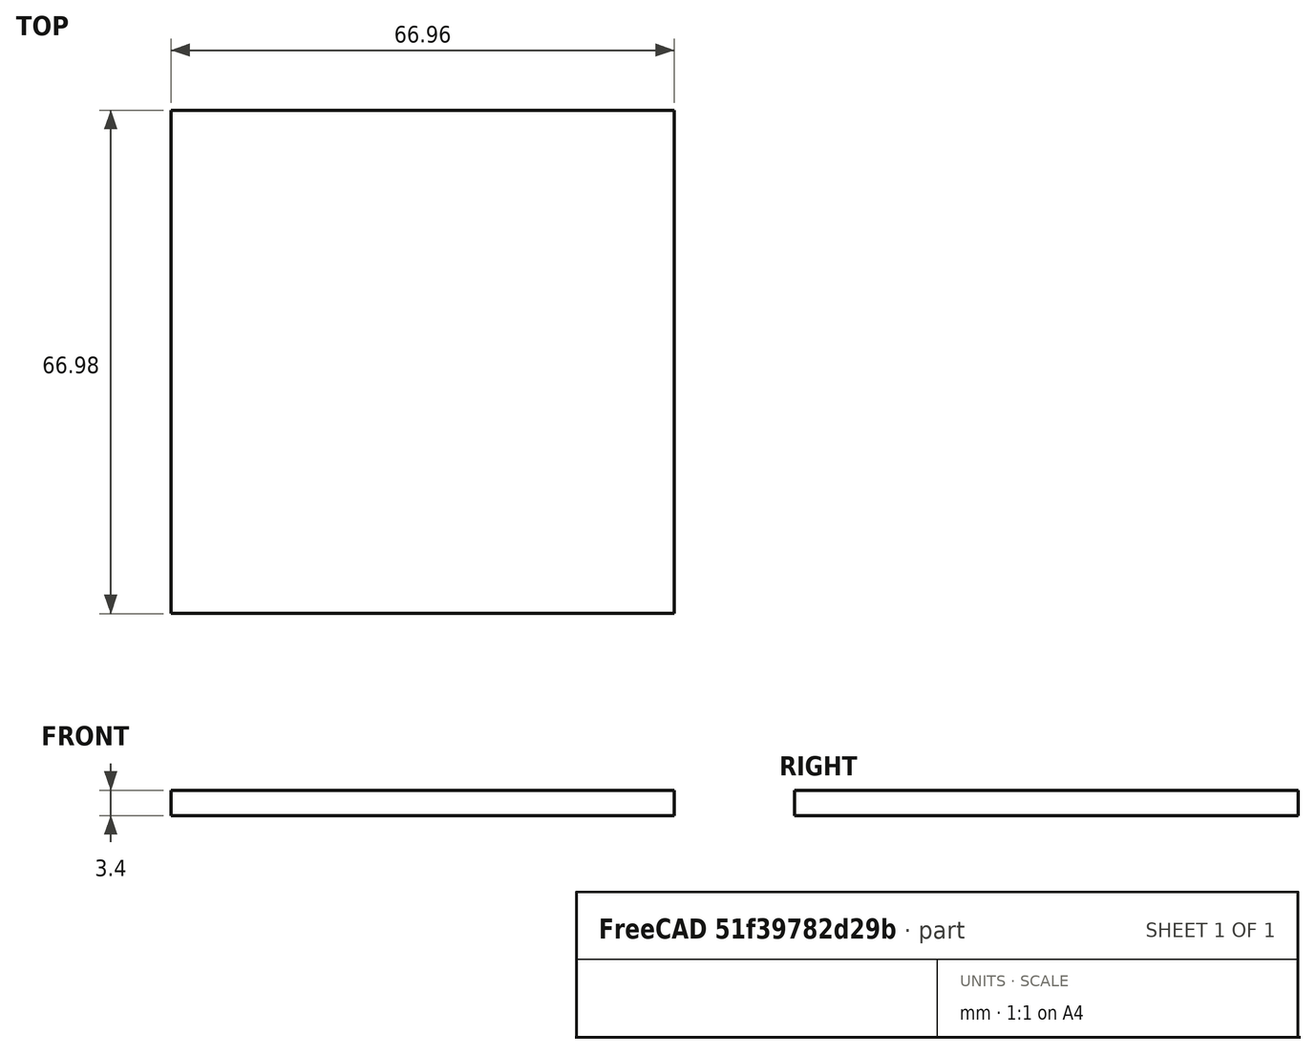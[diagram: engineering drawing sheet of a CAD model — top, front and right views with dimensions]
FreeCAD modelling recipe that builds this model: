
FCSTD DOCUMENT  (FreeCAD 0.17R12703 (Git))
Label: Servospant
License: All rights reserved
LicenseURL: http://en.wikipedia.org/wiki/All_rights_reserved
objects: Path::FeaturePython×8, Part::FeaturePython×2, Part::Feature×1, App::FeaturePython×1, Path::FeatureCompoundPython×1
note: 5 computed .brp shape members not serialized (recipe doc carries the construction recipe); baked Part::Feature solids carry a one-line shape summary decoded from their .brp

FEATURE [Part::Feature] Part__Feature  label="Servospant"
  Placement = pos=(0,0,-3.4) rot=(0,0,1;0rad)
  shape: bbox 66.96 x 67 x 3.4 mm, 43 faces (baked)
FEATURE [App::FeaturePython] SetupSheet  # Path/CAM operation (typed FeaturePython)
  ClearanceHeightExpression = StartDepth+SetupSheet.ClearanceHeightOffset
  ClearanceHeightOffset = 5
  FinalDepthExpression = OpFinalDepth
  HorizRapid = 0
  SafeHeightExpression = StartDepth+SetupSheet.SafeHeightOffset
  SafeHeightOffset = 3
  StartDepthExpression = OpStartDepth
  StepDownExpression = OpToolDiameter
  VertRapid = 0
FEATURE [Part::FeaturePython] Clone  label="Base-Servospant"  # Draft clone (typed FeaturePython)
  AttacherType = Attacher::AttachEngine3D
  Fuse = false
  Objects = -> [Part__Feature]
  PathResource = Base
  Placement = pos=(0,0,-3.4) rot=(0,0,1;0rad)
  Scale = (1,1,1)
FEATURE [Path::FeaturePython] T1__Schaftfraeser_D2  label="T1: Schaftfraeser_D2"  # Path/CAM operation (typed FeaturePython)
  HorizFeed = 400
  HorizRapid = 0
  SpindleDir = 0
  SpindleSpeed = 0
  ToolNumber = 1
  VertFeed = 100
  VertRapid = 0
  expr: VertRapid = SetupSheet.VertRapid
  expr: HorizRapid = SetupSheet.HorizRapid
FEATURE [Part::FeaturePython] Stock  # WARN: FeaturePython — macro-defined, semantics opaque (R4)
  Base = -> Part__Feature
  ExtXneg = 0
  ExtXpos = 0
  ExtYneg = 0
  ExtYpos = 0
  ExtZneg = 0
  ExtZpos = 0
  StockType = FromBase
FEATURE [Path::FeaturePython] Profile_Edges  # Path/CAM operation (typed FeaturePython)
  Active = true
  AreaParams:
    OpenMode = 0
    Angle = 45.0
    MinArcPoints = 4
    Coplanar = 0
    Tolerance = 1e-07
    CleanDistance = 0.0
    PocketExtraOffset = 0.0
    AngleShift = 0.0
    SubjectFill = 0
    RoundPreceision = 0.0
    Simplify = False
    SectionTolerance = 1e-06
    MaxArcPoints = 100
    SectionOffset = 0.0
    Offset = -1.0
    Accuracy = 0.01
    PocketStepover = 0.0
    ClipFill = 0
    ToolRadius = 1.0
    Outline = False
    ClipperScale = 10000000.0
    FromCenter = False
    Explode = False
    EndType = 0
    Shift = 0.0
    ExtraPass = 0
    Project = False
    JoinType = 0
    Thicken = False
    Stepdown = 1.0
    SectionMode = 2
    MiterLimit = 2.0
    Deflection = 0.01
    Reorient = True
    FitArcs = True
    SectionCount = -1
    PocketMode = 0
    Stepover = 0.0
    Unit = 1.0
    Fill = 0
  Base = -> [Clone]
  ClearanceHeight = 5
  Direction = 0
  FinalDepth = -3.7
  JoinType = 0
  MiterLimit = 0.1
  OffsetExtra = 0
  OpFinalDepth = 0
  OpStartDepth = 2
  OpToolDiameter = 2
  PathParams = {'resume_height': 3.0, 'feedrate': 400.0, 'verbose': True, 'orientation': 1, 'return_end': True, 'preamble': False, 'retraction': 5.0, 'feedrate_v': 100.0}
  SafeHeight = 3
  Side = 1
  StartDepth = 0
  StartPoint = (0,0,0)
  StepDown = 2
  ToolController = -> T1__Schaftfraeser_D2
  UseComp = true
  UseStartPoint = false
  expr: ClearanceHeight = StartDepth + SetupSheet.ClearanceHeightOffset
  expr: SafeHeight = StartDepth + SetupSheet.SafeHeightOffset
  expr: StepDown = 2
  expr: FinalDepth = -3.7000000000000002
  expr: StartDepth = 0
FEATURE [Path::FeaturePython] DogboneDressup  # Path/CAM operation (typed FeaturePython)
  Base = -> Profile_Edges
  Custom = 0
  Incision = 0
  Side = 0
  Style = 0
  ToolController = -> T1__Schaftfraeser_D2
FEATURE [Path::FeaturePython] TagDressup  # Path/CAM operation (typed FeaturePython)
  Angle = 45
  Base = -> DogboneDressup
  Height = 1.6
  Positions = (2) [(-6.83404,-25.6047,0),(9.97059,24.5455,0)]
  Radius = 0
  SegmentationFactor = 50
  Width = 4
FEATURE [Path::FeaturePython] Contour  # Path/CAM operation (typed FeaturePython)
  Active = true
  AreaParams:
    OpenMode = 0
    Angle = 45.0
    MinArcPoints = 4
    Coplanar = 2
    Tolerance = 1e-07
    CleanDistance = 0.0
    PocketExtraOffset = 0.0
    AngleShift = 0.0
    SubjectFill = 0
    RoundPreceision = 0.0
    Simplify = False
    SectionTolerance = 1e-06
    MaxArcPoints = 100
    SectionOffset = 0.0
    Offset = 1.0
    Accuracy = 0.01
    PocketStepover = 0.0
    ClipFill = 0
    ToolRadius = 1.0
    Outline = False
    ClipperScale = 10000000.0
    FromCenter = False
    Explode = False
    EndType = 0
    Shift = 0.0
    ExtraPass = 0
    Project = False
    JoinType = 0
    Thicken = False
    Stepdown = 1.0
    SectionMode = 2
    MiterLimit = 2.0
    Deflection = 0.01
    Reorient = True
    FitArcs = True
    SectionCount = -1
    PocketMode = 0
    Stepover = 0.0
    Unit = 1.0
    Fill = 0
  ClearanceHeight = 5
  Direction = 1
  FinalDepth = -3.7
  JoinType = 0
  MiterLimit = 0.1
  OffsetExtra = 0
  OpFinalDepth = -3.4
  OpStartDepth = 0
  OpToolDiameter = 2
  PathParams = {'resume_height': 3.0, 'feedrate': 400.0, 'verbose': True, 'orientation': 0, 'return_end': True, 'preamble': False, 'retraction': 5.0, 'feedrate_v': 100.0}
  SafeHeight = 3
  Side = 0
  StartDepth = 0
  StartPoint = (0,0,0)
  StepDown = 2
  ToolController = -> T1__Schaftfraeser_D2
  UseComp = true
  UseStartPoint = false
  expr: ClearanceHeight = StartDepth + SetupSheet.ClearanceHeightOffset
  expr: SafeHeight = StartDepth + SetupSheet.SafeHeightOffset
  expr: StepDown = 2
  expr: FinalDepth = -3.7000000000000002
  expr: StartDepth = OpStartDepth
FEATURE [Path::FeaturePython] DogboneDressup001  # Path/CAM operation (typed FeaturePython)
  Base = -> Contour
  Custom = 0
  Incision = 0
  Side = 0
  Style = 0
  ToolController = -> T1__Schaftfraeser_D2
FEATURE [Path::FeaturePython] TagDressup001  # Path/CAM operation (typed FeaturePython)
  Angle = 45
  Base = -> DogboneDressup001
  Height = 1.6
  Positions = (3) [(-17.2499,29.8776,0),(-23.3041,-25.4392,0),(34.3091,-3.62143,0)]
  Radius = 0
  SegmentationFactor = 50
  Width = 4
FEATURE [Path::FeatureCompoundPython] Operations  # Path/CAM operation (typed FeaturePython)
  Group = -> [TagDressup,TagDressup001]
  UsePlacements = false
FEATURE [Path::FeaturePython] Job  # Path/CAM operation (typed FeaturePython)
  Base = -> Clone
  GeometryTolerance = 0.01
  Operations = -> Operations
  PostProcessor = 5
  SetupSheet = -> SetupSheet
  Stock = -> Stock
  ToolController = -> [T1__Schaftfraeser_D2]
